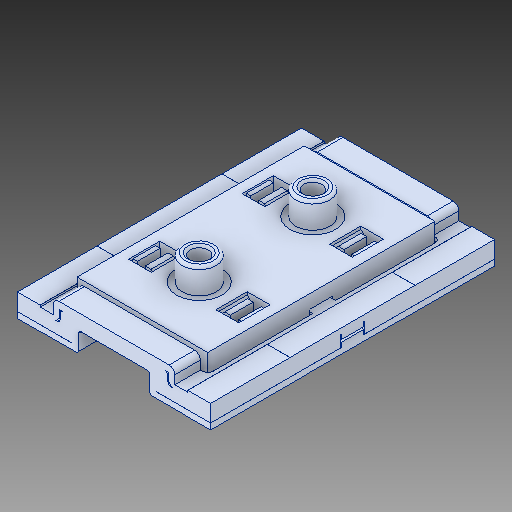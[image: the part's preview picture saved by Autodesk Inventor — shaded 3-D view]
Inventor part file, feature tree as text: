
AUTODESK INVENTOR PART (.ipt)
format: ipt  version: 2018 (Build 220112000, 112)  size: 459,264 bytes
history: native  units: in
note: dims shown in document units (in); Inventor stores cm internally (conversion verified against a paired STEP export)
features: mirror x1
ambient origin geometry x8: Origin, YZ Plane, XZ Plane, XY Plane, X Axis, Y Axis, Z Axis, Center Point
bodies: Solid1 (feature_tree)
feature tree (1):
  mirror  "Mirror3"
